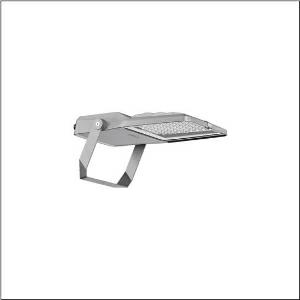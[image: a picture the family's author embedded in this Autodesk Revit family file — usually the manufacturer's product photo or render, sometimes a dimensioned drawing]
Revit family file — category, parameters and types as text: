
# Revit family: floodlight_fl_21_mini___rs12_5xa7771c2b1a_5d2f
name_source: partatom
category: Lighting Fixtures
units: mm (PartAtom-declared; Revit-internal decimal feet)

## family parameters
Cut with Voids When Loaded = No
Host = Face
Light Source = No
Part Type = Normal
Room Calculation Point = No
Round Connector Dimension = Use Diameter
Shared = No

## types (1)
- --- (1 x LED, 12340 lm, 87.2 W, 3000K)
    Apparent Load = 87 VA
    CIE Flux Codes = 79 92 99 100 100
    Color Rendering = 70
    Color Temperature = 3000K
    Default Elevation = 1800 mm
    Description = Floodlight FL 21 mini, floodlight, primary light control with lens, of PMMA, primary optical cover: protective disc, of toughened safety glass, transparent, light distribution: RS12, light emission: direct distribution, installation type: surface-mounted, LED, High Power LED, rated luminous flux: 12.340lm, luminous efficacy: 142lm/W, light colour: 730, colour temperature: 3000K, control gear: ECG iQ, control: Auto-Match, Temp-Guard, Lumen-Switch, Night-Set, Smart-Wire, Light-Fading, Desk-Remote (wireless, voltage-free reading and setting of iQ features in the workshop via application-optimized NFC function/RFID function), optimised constant luminous flux control (CLO 2.0), with terminal, 6-pole, mains connection: 220..240V, AC, 50/60Hz, start of lifetime: 87W, end of lifetime: 92W, reduction: 40W, luminaire housing, of diecast aluminium, powder-coated, Siteco® metallic grey (DB 702S), corrosivity category C5 according to DIN EN ISO 12944, mounting bracket, of steel, galvanised, powder-coated, Siteco® metallic grey (DB 702S), protection rating (complete): IP66, insulation class (complete): insulation class II (safety insulation), certification: CE, ENEC, VDE, protection symbol: D, impact resistance: IK08, permissible operating ambient temperature: -40..+40°C, permissible operating ambient temperature for outdoor applications: -40..+50°C, standard: DIN EN 12944, packaging unit: 1 piece

Light Distribution: RS12
    Height = 70 mm
    Lamp = 1 x LED
    Lamp Light Flux = 12340 lm
    Lamp Power = 87.2 W
    Lamp count = 1
    Length = 485 mm
    Luminous efficacy = 142 lm/W
    Manufacturer = Siteco
    ModVariant = No
    Model = 5XA7771C2B1A
    Number of Poles = 1
    OnlyDefault = Yes
    Power Factor = 1
    Product Name = Floodlight FL 21 mini | RS12
    Product group = floodlight | pylon top
    ProductGroupID = 6101
    Protection Class = Protection class II
    Protection Degree = IP 66
    RLX_Detail_Level = 1
    RlxData = <blob elided: 90893 chars, md5=a63b568c>
    Socket = socket
    Standby Power = 0 W
    System Light Flux = 12340 lm
    System Power = 87 W
    Type Comments = factory setting: luminous flux: 100 % | dim-lin: 254 | 456 mA
    Type Image = l_1006845.jpg
    URL = http://relux.com
    VarID = @adj_078811
    Voltage = 0 V
    Weight = 0.00 kg
    Width = 337 mm

## geometry (parser evidence)
native form markers: Blend x4, Sweep x13
no freeform markers — native parametric forms only
